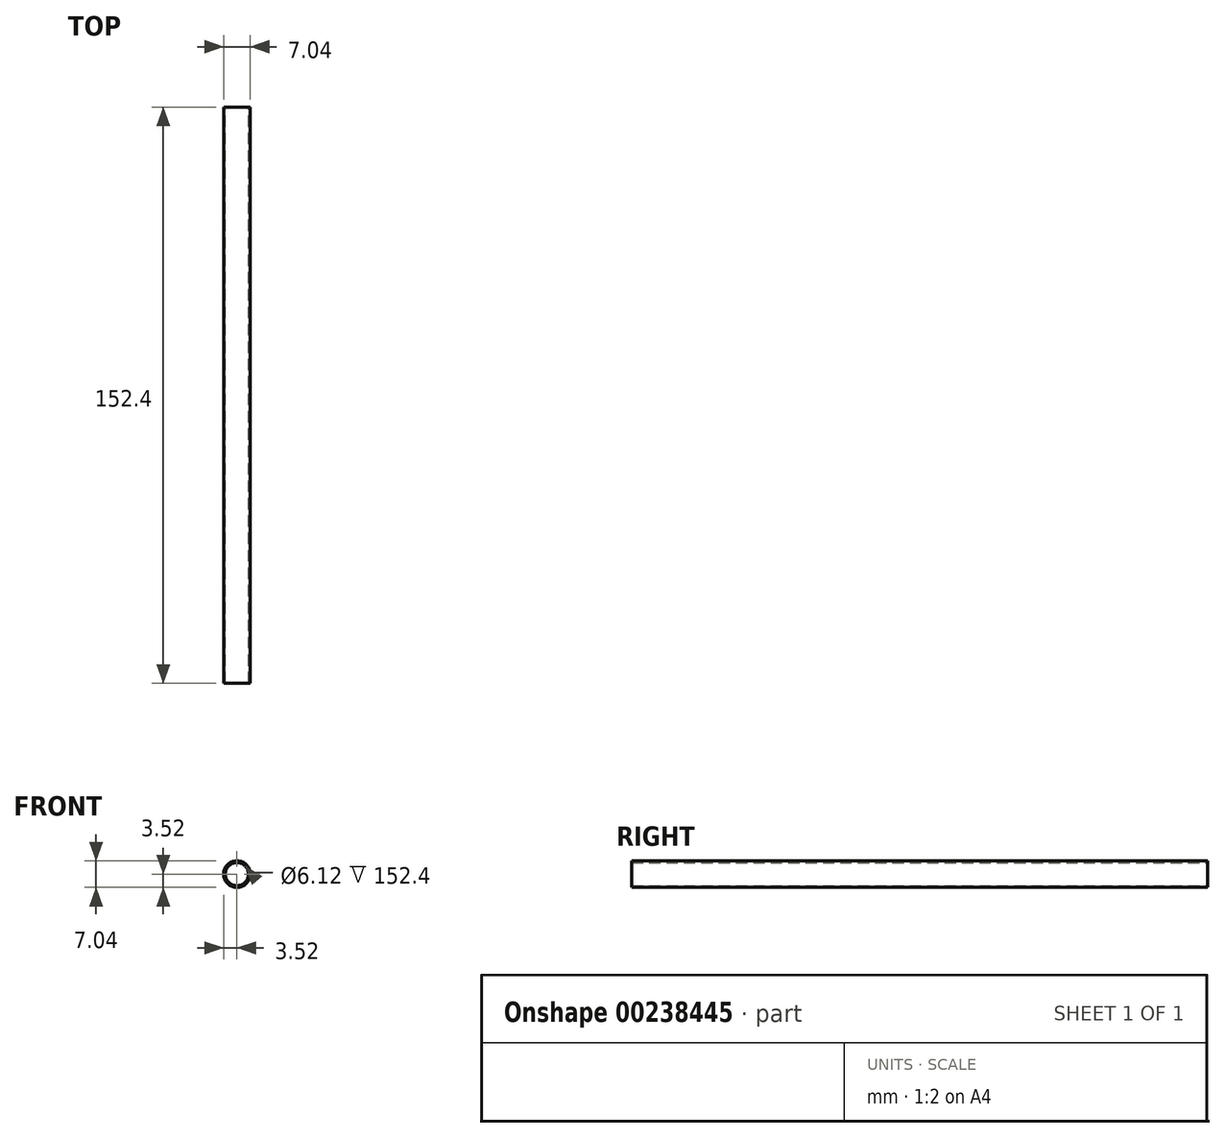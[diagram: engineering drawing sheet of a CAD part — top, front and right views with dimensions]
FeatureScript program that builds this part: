
annotation { "Feature Type Name" : "Feature", "Feature Type Description" : "" }
export const myFeature = defineFeature(function(context is Context, id is Id, definition is map)
    precondition{}
    {
        {
            var Q0;
            Q0=qCreatedBy(makeId("Front.planeOp"),FACE);
            var sketch = newSketch(context, id + "F0", { "sketchPlane" : qUnion([Q0])});
            skCircle(sketch, "E0", {"center": v(0, 0) * mm, "radius": 3.52 * mm});
            skSolve(sketch);
        }
        {
            var Q0;
            Q0=makeQuery(id+"F0.imprint","IMPRINT",FACE,{"disambiguationData":[TD([[makeQuery(id+"F0.imprint","IMPRINT",EDGE,{"derivedFrom":sQuery(id+"F0.wireOp",EDGE,"E0")}),1.0]])]});
            extrude(context, id + "F1", {"entities" : qUnion([Q0]), "depth" : 152.4 * mm});
        }
        {
            var Q0;
            Q0=qCreatedBy(makeId("Front.planeOp"),FACE);
            var sketch = newSketch(context, id + "F2", { "sketchPlane" : qUnion([Q0])});
            skCircle(sketch, "E1", {"center": v(0, 0) * mm, "radius": 3.06 * mm});
            skSolve(sketch);
        }
        {
            var Q0;
            Q0=makeQuery(id+"F2.imprint","IMPRINT",FACE,{"disambiguationData":[TD([[makeQuery(id+"F2.imprint","IMPRINT",EDGE,{"derivedFrom":sQuery(id+"F2.wireOp",EDGE,"E1")}),1.0]])]});
            extrude(context, id + "F3", {"entities" : qUnion([Q0]), "operationType" : NewBodyOperationType.REMOVE, "depth" : 304.8 * mm});
        }
    });
